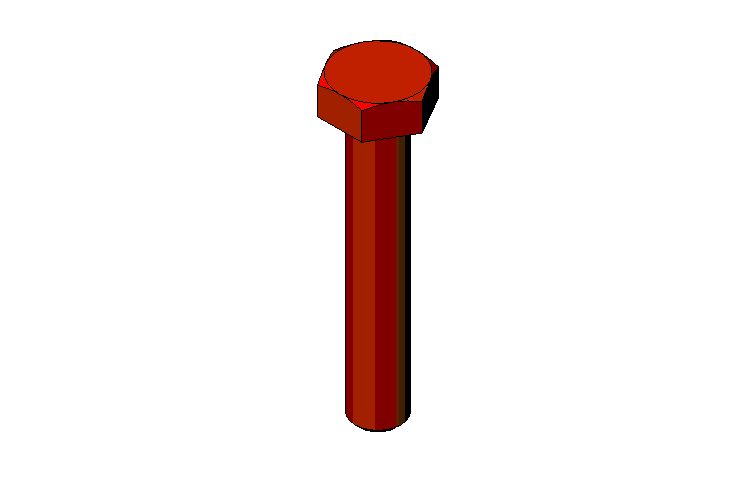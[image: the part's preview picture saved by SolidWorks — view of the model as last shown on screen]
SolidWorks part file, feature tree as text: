
SOLIDWORKS PART (.sldprt)
format: sldprt  version: not decoded by parser v0  size: 178,688 bytes
history: native  units: mm
features: sketch x4, plane x3, material x1, extrude x1, chamfer x1, revolve x1, cut_extrude x1 (+10 scaffold rows collapsed)
feature tree (22):
  scaffold x10  (default folders/planes/origin — collapsed)
  material  "Matériau <non spécifié>"
  plane  "Plan1"
  plane  "Plan2"
  plane  "Plan3"
  sketch  "Esquisse2"  dims[Diamètre nominal=6.0mm]
  extrude  "Base-Extrusion"  Depth=35mm Longueur sous tête=35mm
  chamfer  "Chanfrein1"  Distance=0.6mm Angle=45deg
  sketch  "Esquisse5"  dims[c1.Hauteur tête=4.0mm c1.Cote sur plats=10.0mm c1.D3=~2.780036mm c2.D3=30.0deg c2.D4=5.0mm c2.D1=~7.071068mm]
  revolve  "Boss.-Révol.1"  Angle=360deg
  sketch  "Esquisse6"  dims[c1.D1=5.5mm c2.D1=30.0deg c2.D2=2.75mm c3.D2=30.0deg c3.D1=2.75mm c4.D1=30.0deg c4.D2=~3.889087mm c5.D2=30.0deg c5.D3=~1.587713mm c6.D3=120.0deg]
  cut_extrude  "Enlèv. mat.-Extru.1"  Depth=4mm Hauteur tête=4mm
  sketch  "Esquisse3"
decode coverage: 7 of 8 modeling features carry decoded parameters
note: ~ marks probable driven/reference dimensions
note: suppression state not decoded; provenance and decode notes live in map.json
